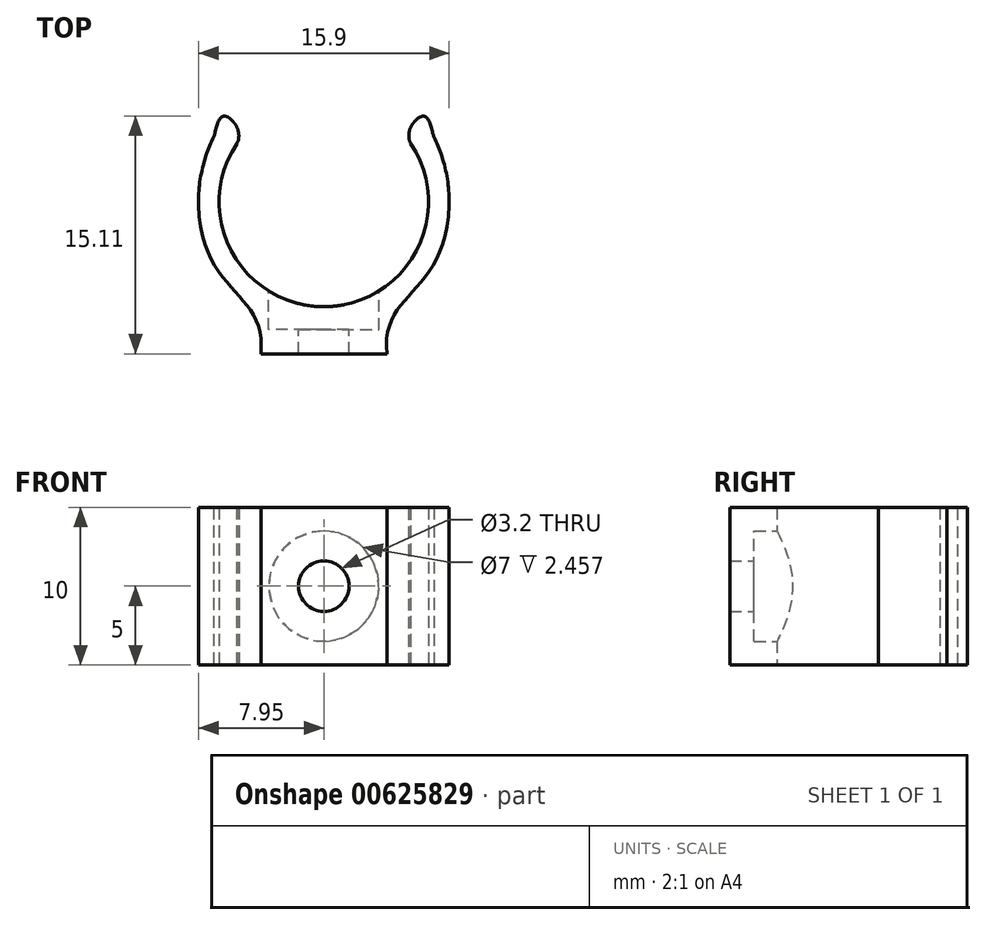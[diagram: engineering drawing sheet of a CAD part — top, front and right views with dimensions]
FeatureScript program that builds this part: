
annotation { "Feature Type Name" : "Feature", "Feature Type Description" : "" }
export const myFeature = defineFeature(function(context is Context, id is Id, definition is map)
    precondition{}
    {
        {
            var Q0;
            Q0=qCreatedBy(makeId("Top.planeOp"),FACE);
            var sketch = newSketch(context, id + "F0", { "sketchPlane" : qUnion([Q0])});
            skCircle(sketch, "E0", {"center": v(0, 0) * mm, "radius": 6.65 * mm});
            skLineSegment(sketch, "E1", {"start": v(0, -9.65) * mm, "end": v(-4, -9.65) * mm});
            skLineSegment(sketch, "E2", {"start": v(-7.95, 0) * mm, "end": v(-7.95, 0.2) * mm});
            skLineSegment(sketch, "E3.MirrorCS", {"start": v(-7.95, 0) * mm, "end": v(-7.95, -0.2) * mm});
            skFitSpline(sketch, "E4", {"points": [v(-7.95, -0.2) * mm, v(-4, -9.65) * mm], "startDerivative": vector(0.5, -17.16) * mm, "endDerivative": vector(-1.24, -12.15) * mm});
            skLineSegment(sketch, "E5.MirrorCS", {"start": v(0, -9.65) * mm, "end": v(4, -9.65) * mm});
            skFitSpline(sketch, "E6.MirrorCS", {"points": [v(7.95, -0.2) * mm, v(4, -9.65) * mm], "startDerivative": vector(-0.5, -17.16) * mm, "endDerivative": vector(1.24, -12.15) * mm});
            skLineSegment(sketch, "E7.MirrorCS", {"start": v(7.95, 0) * mm, "end": v(7.95, 0.2) * mm});
            skLineSegment(sketch, "E8.MirrorCS", {"start": v(7.95, 0) * mm, "end": v(7.95, -0.2) * mm});
            skLineSegment(sketch, "E9", {"start": v(-6.65, 0) * mm, "end": v(-6.65, 5.28) * mm, "construction": true});
            skLineSegment(sketch, "E10", {"start": v(-5.55, 0) * mm, "end": v(-5.55, 5.39) * mm, "construction": true});
            skFitSpline(sketch, "E11", {"points": [v(-5.55, 3.66) * mm, v(-5.94, 5.18) * mm, v(-7.95, 0.2) * mm], "startDerivative": vector(2.97, 4.1) * mm, "endDerivative": vector(0.08, -10.17) * mm});
            skFitSpline(sketch, "E12.MirrorCS", {"points": [v(5.55, 3.66) * mm, v(5.94, 5.18) * mm, v(7.95, 0.2) * mm], "startDerivative": vector(-2.97, 4.1) * mm, "endDerivative": vector(-0.08, -10.17) * mm});
            skFitSpline(sketch, "E13", {"points": [v(-5.55, 4.83) * mm, v(-7, 4.13) * mm], "startDerivative": vector(-3.48, 4.91) * mm, "endDerivative": vector(-0.43, -0.9) * mm});
            skFitSpline(sketch, "E14.MirrorCS", {"points": [v(5.55, 4.83) * mm, v(7, 4.13) * mm], "startDerivative": vector(3.48, 4.91) * mm, "endDerivative": vector(0.43, -0.9) * mm});
            skSolve(sketch);
        }
        {
            var Q0;
            Q0=makeQuery(id+"F0.imprint","IMPRINT",FACE,{"disambiguationData":[TD([[makeQuery(id+"F0.imprint","IMPRINT",EDGE,{"derivedFrom":sQuery(id+"F0.wireOp",EDGE,"E1")}),-1.0]])]});
            var Q1;
            {var subQ0=sQuery(id+"F0.wireOp",EDGE,"E13");var subQ1=sQuery(id+"F0.wireOp",EDGE,"E11");var subQ2=makeQuery(id+"F0.imprint","INTERSECT",VERTEX,{"disambiguationData":[OD(1.0)],"derivedFrom":[subQ1,subQ0]});Q1=makeQuery(id+"F0.imprint","IMPRINT",FACE,{"disambiguationData":[TD([[makeQuery(id+"F0.imprint","IMPRINT",EDGE,{"disambiguationData":[TD([[subQ2,1.0]])],"derivedFrom":subQ1}),-1.0]])]});}
            var Q2;
            {var subQ0=sQuery(id+"F0.wireOp",EDGE,"E14.MirrorCS");var subQ1=sQuery(id+"F0.wireOp",EDGE,"E12.MirrorCS");var subQ2=makeQuery(id+"F0.imprint","INTERSECT",VERTEX,{"disambiguationData":[OD(1.0)],"derivedFrom":[subQ1,subQ0]});Q2=makeQuery(id+"F0.imprint","IMPRINT",FACE,{"disambiguationData":[TD([[makeQuery(id+"F0.imprint","IMPRINT",EDGE,{"disambiguationData":[TD([[subQ2,1.0]])],"derivedFrom":subQ1}),1.0]])]});}
            extrude(context, id + "F1", {"entities" : qUnion([Q0, Q1, Q2]), "depth" : 10 * mm, "offsetDistance" : 25 * mm});
        }
        {
            var Q0;
            Q0=qCreatedBy(makeId("Front.planeOp"),FACE);
            var sketch = newSketch(context, id + "F2", { "sketchPlane" : qUnion([Q0])});
            skCircle(sketch, "E15", {"center": v(0, 5) * mm, "radius": 1.6 * mm});
            skCircle(sketch, "E16", {"center": v(0, 5) * mm, "radius": 3.5 * mm});
            skLineSegment(sketch, "E17", {"start": v(0, 0) * mm, "end": v(2, 0) * mm});
            skSolve(sketch);
        }
        {
            var Q0;
            Q0=makeQuery(id+"F2.imprint","IMPRINT",FACE,{"disambiguationData":[TD([[makeQuery(id+"F2.imprint","IMPRINT",EDGE,{"derivedFrom":sQuery(id+"F2.wireOp",EDGE,"E15")}),1.0]])]});
            extrude(context, id + "F3", {"entities" : qUnion([Q0]), "operationType" : NewBodyOperationType.REMOVE, "depth" : 23.7 * mm, "offsetDistance" : 25 * mm});
        }
        {
            var Q0;
            Q0=makeQuery(id+"F2.imprint","IMPRINT",FACE,{"disambiguationData":[TD([[makeQuery(id+"F2.imprint","IMPRINT",EDGE,{"derivedFrom":sQuery(id+"F2.wireOp",EDGE,"E15")}),-1.0]])]});
            extrude(context, id + "F4", {"entities" : qUnion([Q0]), "operationType" : NewBodyOperationType.REMOVE, "depth" : 8.1 * mm, "offsetDistance" : 25 * mm});
        }
    });
